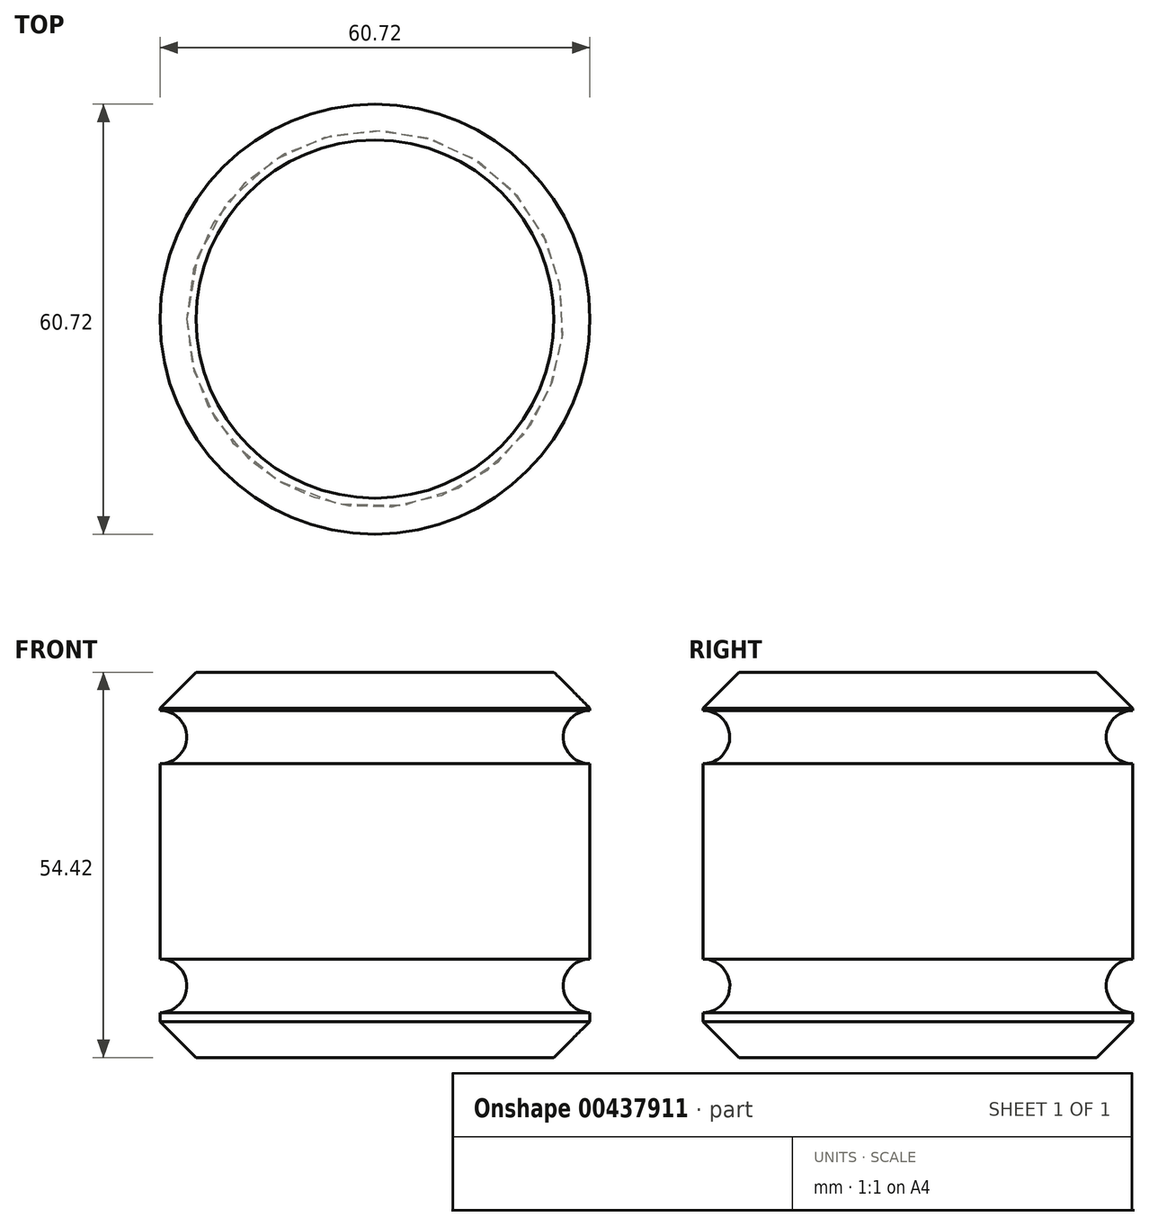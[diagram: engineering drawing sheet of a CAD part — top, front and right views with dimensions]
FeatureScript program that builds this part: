
annotation { "Feature Type Name" : "Feature", "Feature Type Description" : "" }
export const myFeature = defineFeature(function(context is Context, id is Id, definition is map)
    precondition{}
    {
        {
            var Q0;
            Q0=qCreatedBy(makeId("Front.planeOp"),FACE);
            var sketch = newSketch(context, id + "F0", { "sketchPlane" : qUnion([Q0])});
            skLineSegment(sketch, "E0.bottom", {"start": v(0, 0) * mm, "end": v(-30.36, 0) * mm});
            skLineSegment(sketch, "E0.top", {"start": v(0, 54.42) * mm, "end": v(-30.36, 54.42) * mm});
            skLineSegment(sketch, "E0.left", {"start": v(0, 0) * mm, "end": v(0, 6.35) * mm});
            skLineSegment(sketch, "E0.right", {"start": v(-30.36, 0) * mm, "end": v(-30.36, 54.42) * mm});
            skArc(sketch, "E1", {"start": v(0, 49.02) * mm, "mid": v(-3.77, 45.26) * mm, "end": v(0, 41.5) * mm});
            skArc(sketch, "E2", {"start": v(0, 13.9) * mm, "mid": v(-3.77, 10.12) * mm, "end": v(0, 6.35) * mm});
            skLineSegment(sketch, "E3.trimOffspring", {"start": v(0, 49.02) * mm, "end": v(0, 54.42) * mm});
            skLineSegment(sketch, "E4.trimOffspring", {"start": v(0, 13.9) * mm, "end": v(0, 41.5) * mm});
            skSolve(sketch);
        }
        {
            var Q0;
            Q0=makeQuery(id+"F0.imprint","IMPRINT",FACE,{"disambiguationData":[TD([[makeQuery(id+"F0.imprint","IMPRINT",EDGE,{"derivedFrom":sQuery(id+"F0.wireOp",EDGE,"E0.bottom")}),-1.0]])]});
            var Q1;
            Q1=sQuery(id+"F0.wireOp",EDGE,"E0.right");
            revolve(context, id + "F1", {"entities" : qUnion([Q0]), "axis" : qUnion([Q1]), "revolveType" : RevolveType.FULL});
        }
        {
            var Q0;
            Q0=makeQuery(id+"F1.opRevolve","SWEPT_EDGE",EDGE,{"disambiguationData":[OSD([sQuery(id+"F0.wireOp",EDGE,"E0.top"),sQuery(id+"F0.wireOp",EDGE,"E3.trimOffspring")])]});
            var Q1;
            Q1=makeQuery(id+"F1.opRevolve","SWEPT_EDGE",EDGE,{"disambiguationData":[OSD([sQuery(id+"F0.wireOp",EDGE,"E0.bottom"),sQuery(id+"F0.wireOp",EDGE,"E0.left")])]});
            chamfer(context, id + "F2", {"entities" : qUnion([Q0, Q1]), "width" : 5.08 * mm, "tangentPropagation" : true});
        }
    });
